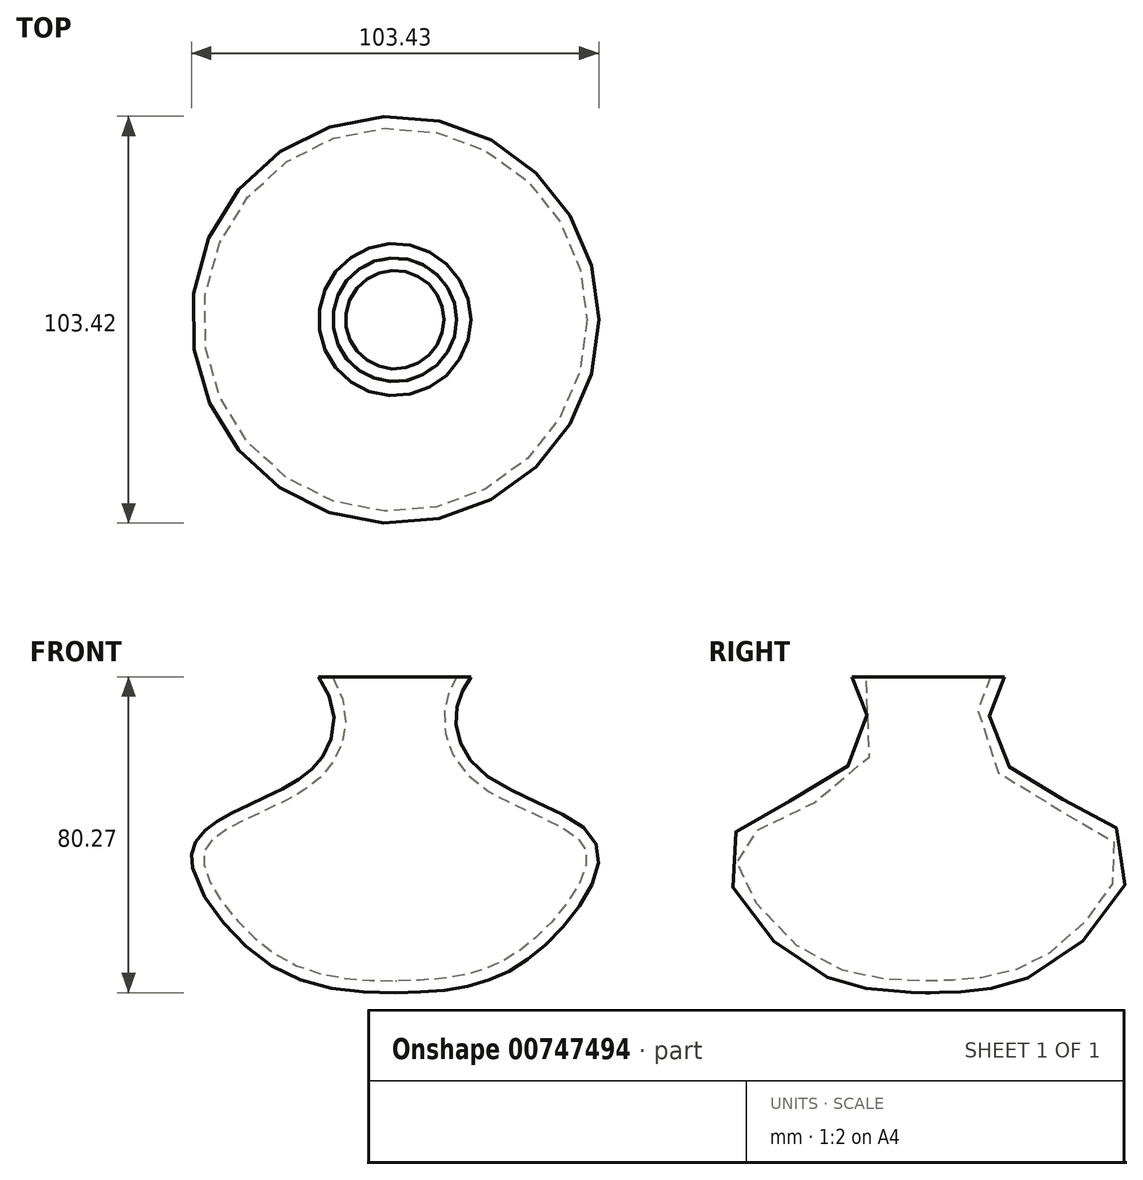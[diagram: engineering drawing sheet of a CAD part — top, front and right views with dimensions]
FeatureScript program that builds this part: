
annotation { "Feature Type Name" : "Feature", "Feature Type Description" : "" }
export const myFeature = defineFeature(function(context is Context, id is Id, definition is map)
    precondition{}
    {
        {
            var Q0;
            Q0=qCreatedBy(makeId("Front.planeOp"),FACE);
            var sketch = newSketch(context, id + "F0", { "sketchPlane" : qUnion([Q0])});
            skFitSpline(sketch, "E0", {"points": [v(22.6, 46.21) * mm, v(15.82, 34.16) * mm, v(22.6, 17.34) * mm, v(50.97, 0) * mm, v(41.43, -23.1) * mm, v(19.83, -36.4) * mm, v(-10.3, -38.16) * mm], "startDerivative": vector(-69.59, -87.18) * mm, "endDerivative": vector(-169.3, 4.18) * mm});
            skLineSegment(sketch, "E1", {"start": v(-10.74, 41.94) * mm, "end": v(27.62, 41.94) * mm});
            skLineSegment(sketch, "E2", {"start": v(0, 47.72) * mm, "end": v(0.3, -62.27) * mm});
            skSolve(sketch);
        }
        {
            var Q0;
            {var subQ0=sQuery(id+"F0.wireOp",EDGE,"E1");var subQ1=sQuery(id+"F0.wireOp",EDGE,"E0");var subQ2=makeQuery(id+"F0.imprint","INTERSECT",VERTEX,{"derivedFrom":[subQ1,subQ0]});Q0=makeQuery(id+"F0.imprint","IMPRINT",FACE,{"disambiguationData":[TD([[makeQuery(id+"F0.imprint","IMPRINT",EDGE,{"disambiguationData":[TD([[subQ2,-1.0]])],"derivedFrom":subQ1}),-1.0]])]});}
            var Q1;
            Q1=sQuery(id+"F0.wireOp",EDGE,"E2");
            revolve(context, id + "F1", {"surfaceOperationType" : NewSurfaceOperationType.NEW, "entities" : qUnion([Q0]), "axis" : qUnion([Q1]), "revolveType" : RevolveType.FULL});
        }
        {
            var Q0;
            Q0=makeQuery(id+"F1.opRevolve","SWEPT_FACE",FACE,{"disambiguationData":[OSD([sQuery(id+"F0.wireOp",EDGE,"E1")])]});
            shell(context, id + "F2", {"entities" : qUnion([Q0]), "thickness" : 3 * mm});
        }
    });
